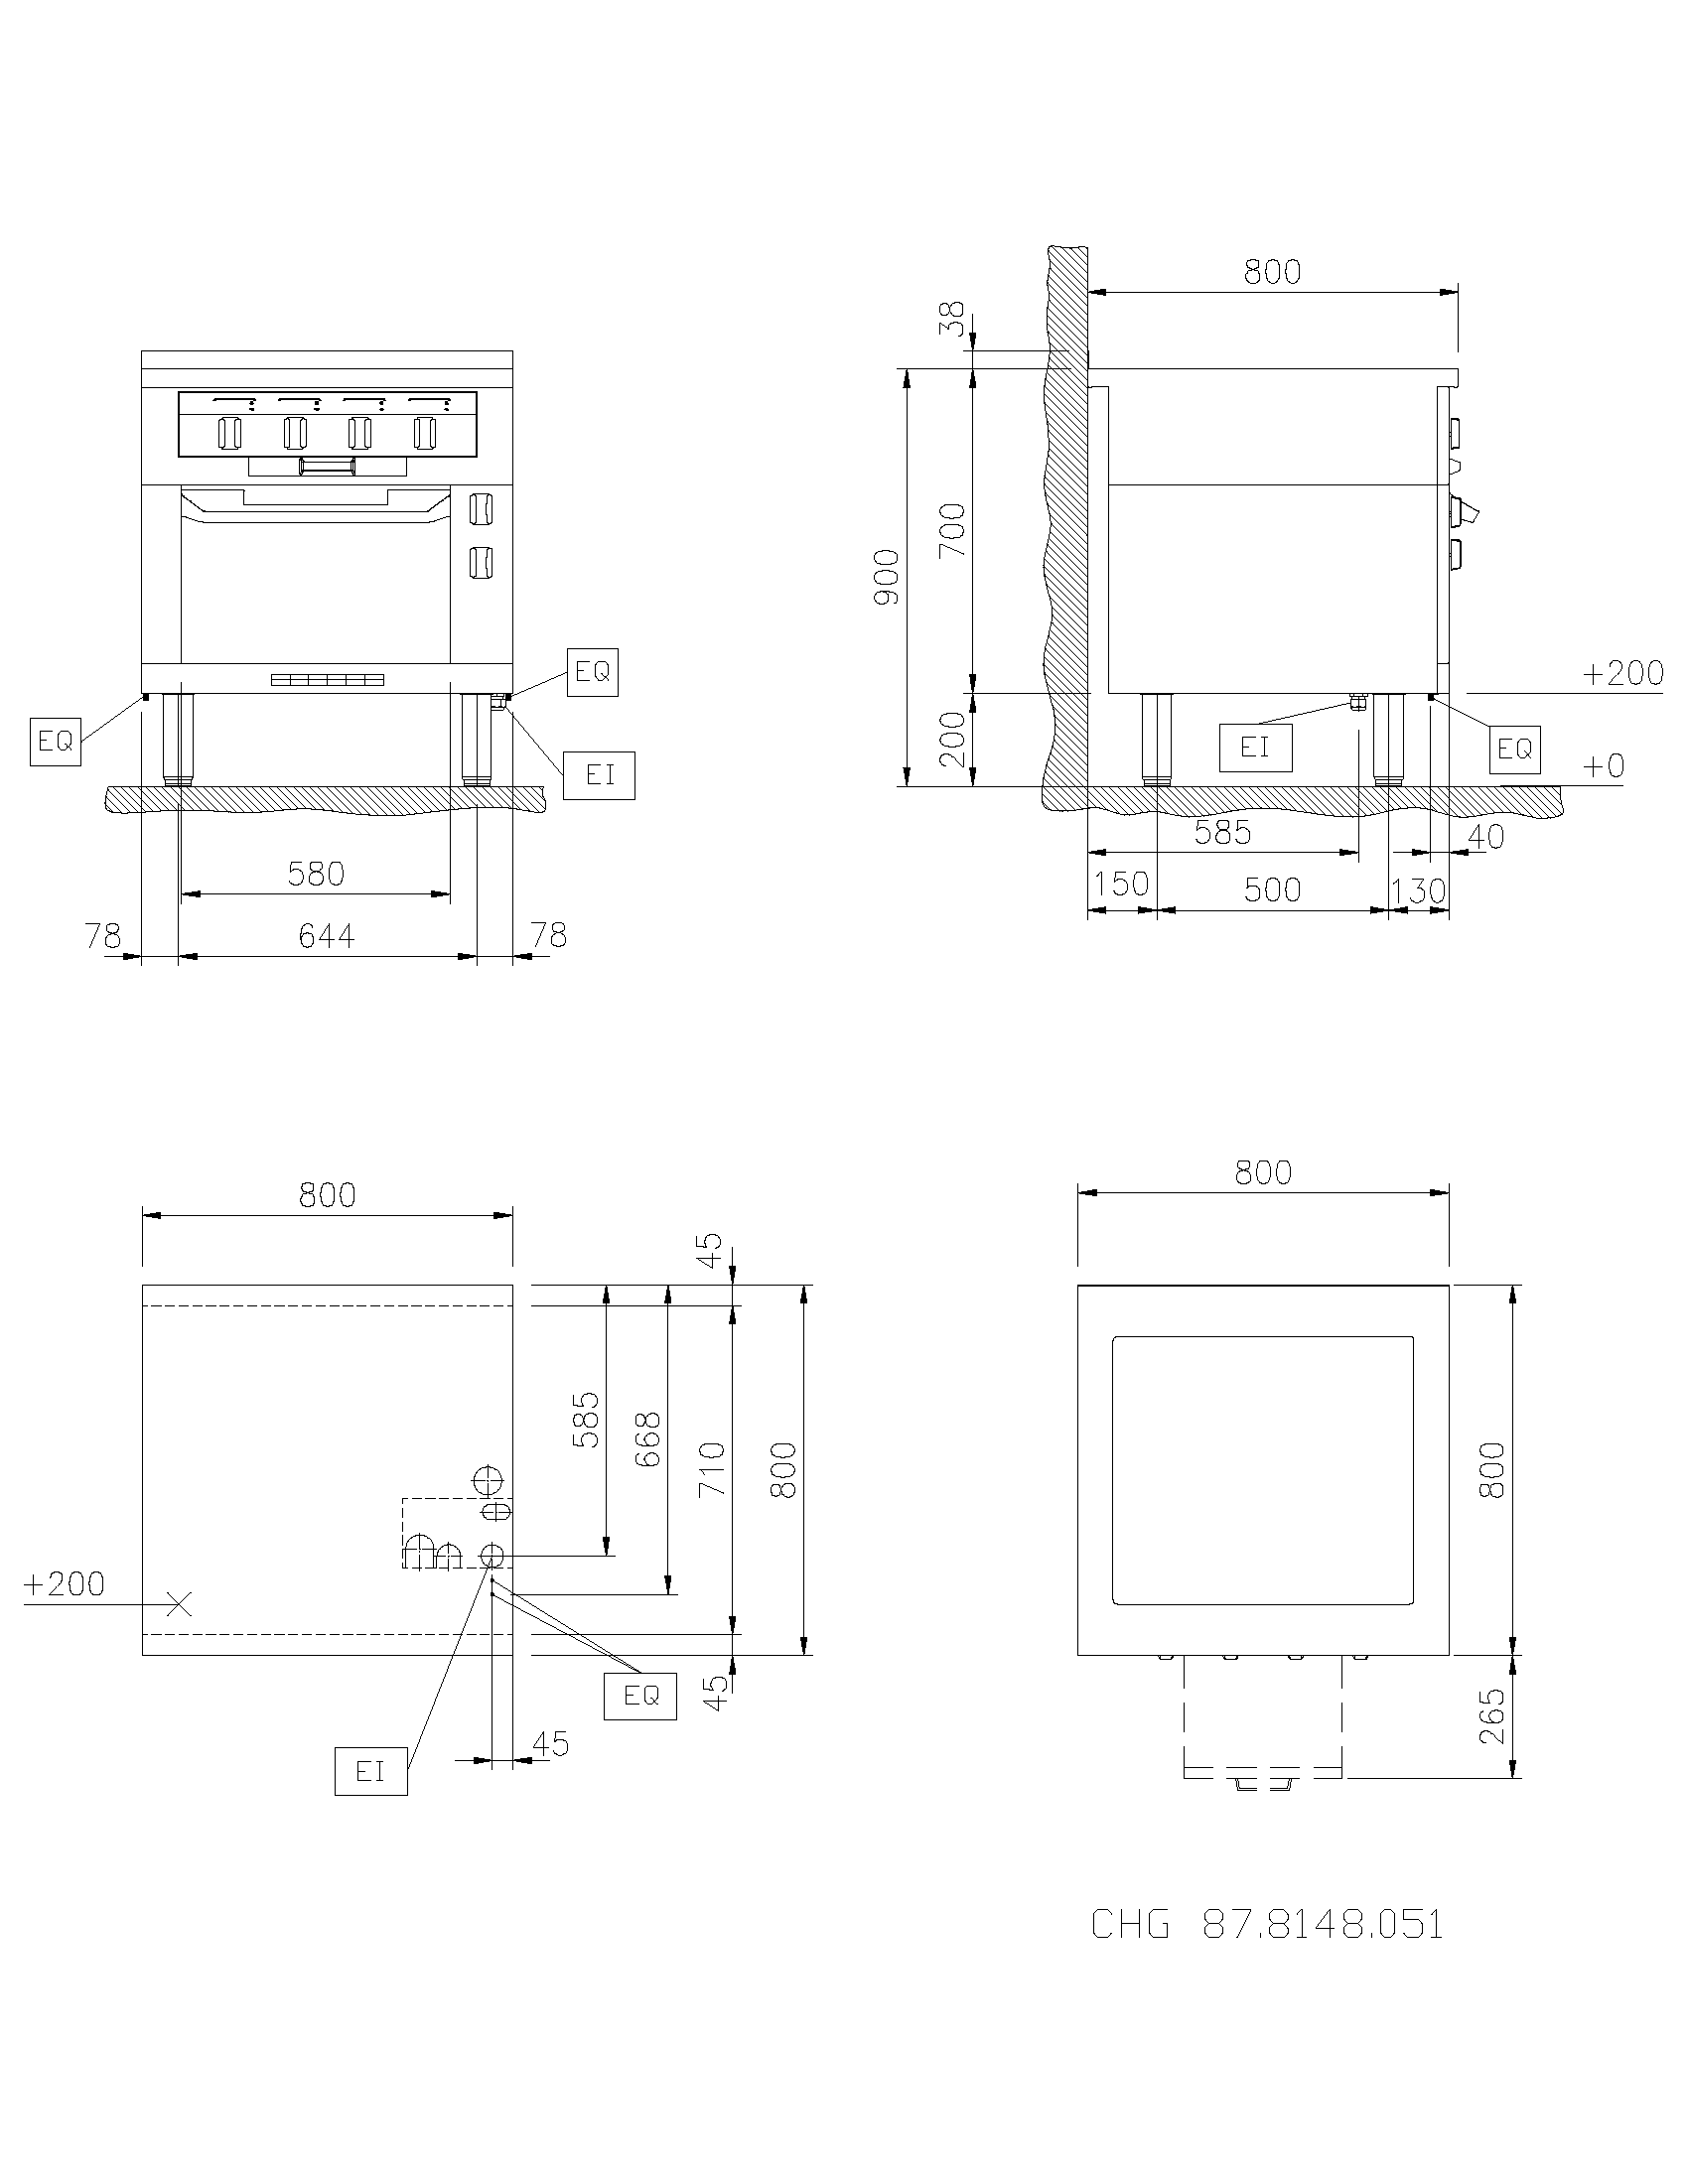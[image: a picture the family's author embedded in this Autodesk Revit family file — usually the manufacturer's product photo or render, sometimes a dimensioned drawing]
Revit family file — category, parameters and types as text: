
# Revit family: QF_ELECTROLUXPROFESSIONAL_588432_MAINFCH8AO
name_source: partatom
category: Attrezzature speciali
units: mm (PartAtom-declared; Revit-internal decimal feet)

## family parameters
Basato su piano di lavoro = No
Condiviso = No
Punto di calcolo locali = No
Quota connettore circolare = Usa diametro
Sempre verticale = Sì
Taglio con vuoti quando caricato = No
Tipo di parte = Normale

## types (1)
- Standard
    Accessory = Sì
    Cold Water Size = 0"
    Compressed Air Pressure = 0.00 psi
    Compressed Air Size = 0"
    Compressed Air Volume = 0 GPM
    Condensate Return Size = 0"
    Cycle = 50 Hz
    Depth Actual = 800 mm  [stored 2.62467 ft]
    Descrizione = INDUCTION,4Z,ST.OVEN PASS,2S,800X800X800
    Direct Waste Size = 0"
    Gas Input Pressure = 0.0
    Gas KW = 0
    Gas Size = 0"
    HP = 33.5 HP
    Height Actual = 800 mm  [stored 2.62467 ft]
    Hot Water Size = 0"
    Item Number = 588432
    Length Actual = 800 mm  [stored 2.62467 ft]
    Modello = MAINFCH8AO
    Phase = 3
    Produttore = Electrolux Professional
    Prospetto di default = 0 mm  [stored 0 ft]
    Refrigerant Compressor Remote = Sì
    Refrigeration Liquid Line Size = 0 mm  [stored 0 ft]
    Refrigeration Suction Line Size = 0 mm  [stored 0 ft]
    Steam Consumption per Hour = 0
    Steam Supply Maximum Pressure = 0.00 psi
    Steam Supply Minimum Pressure = 0.00 psi
    Steam Supply Size = 0"
    URL = https://www.electroluxprofessional.com
    URL Manufacturer = https://www.electroluxprofessional.com
    Volts = 400 V
    Watts = 25000 W
    Weight = 125.00 kg

note: source unit labels omitted for Gas Input Pressure — the stored unit's dimension contradicts the parameter name (converter mislabeling)

note: [stored X ft] marks values corroborated as IEEE doubles in the binary element streams (Revit-internal decimal feet)

## geometry (parser evidence)
native form markers: Blend x24, Sweep x10
no freeform markers — native parametric forms only
